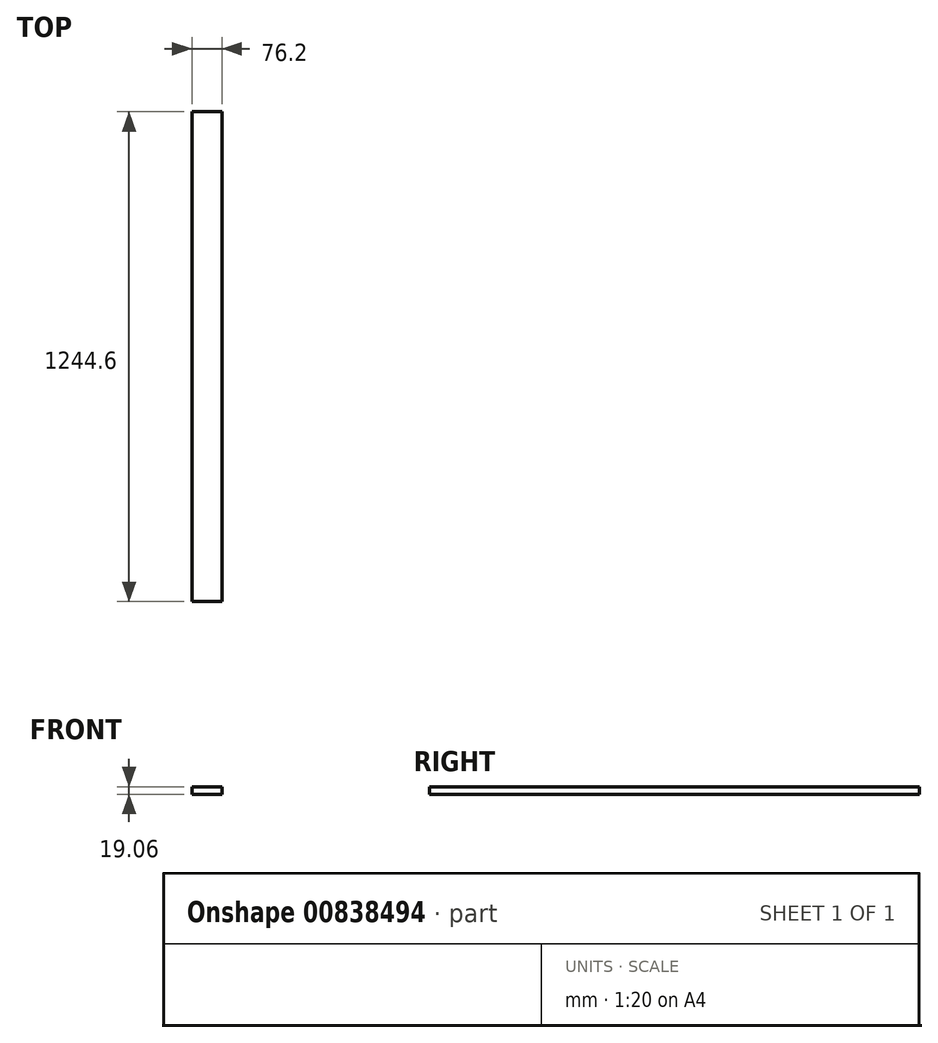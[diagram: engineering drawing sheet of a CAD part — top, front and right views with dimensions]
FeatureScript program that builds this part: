
annotation { "Feature Type Name" : "Feature", "Feature Type Description" : "" }
export const myFeature = defineFeature(function(context is Context, id is Id, definition is map)
    precondition{}
    {
        {
            var Q0;
            Q0=qCreatedBy(makeId("Right.planeOp"),FACE);
            var sketch = newSketch(context, id + "F0", { "sketchPlane" : qUnion([Q0])});
            skLineSegment(sketch, "E0.bottom", {"start": v(-622.3, -9.53) * mm, "end": v(622.3, -9.53) * mm});
            skLineSegment(sketch, "E0.top", {"start": v(-622.3, 9.53) * mm, "end": v(622.3, 9.53) * mm});
            skLineSegment(sketch, "E0.left", {"start": v(-622.3, -9.53) * mm, "end": v(-622.3, 9.53) * mm});
            skLineSegment(sketch, "E0.right", {"start": v(622.3, -9.53) * mm, "end": v(622.3, 9.53) * mm});
            skPoint(sketch, "E0.middle", {"position": v(0, 0) * mm});
            skSolve(sketch);
        }
        {
            var Q0;
            Q0 = qSketchRegion(id + "F0", true);
            extrude(context, id + "F1", {"entities" : qUnion([Q0]), "depth" : 76.2 * mm, "offsetDistance" : 25.4 * mm});
        }
    });
